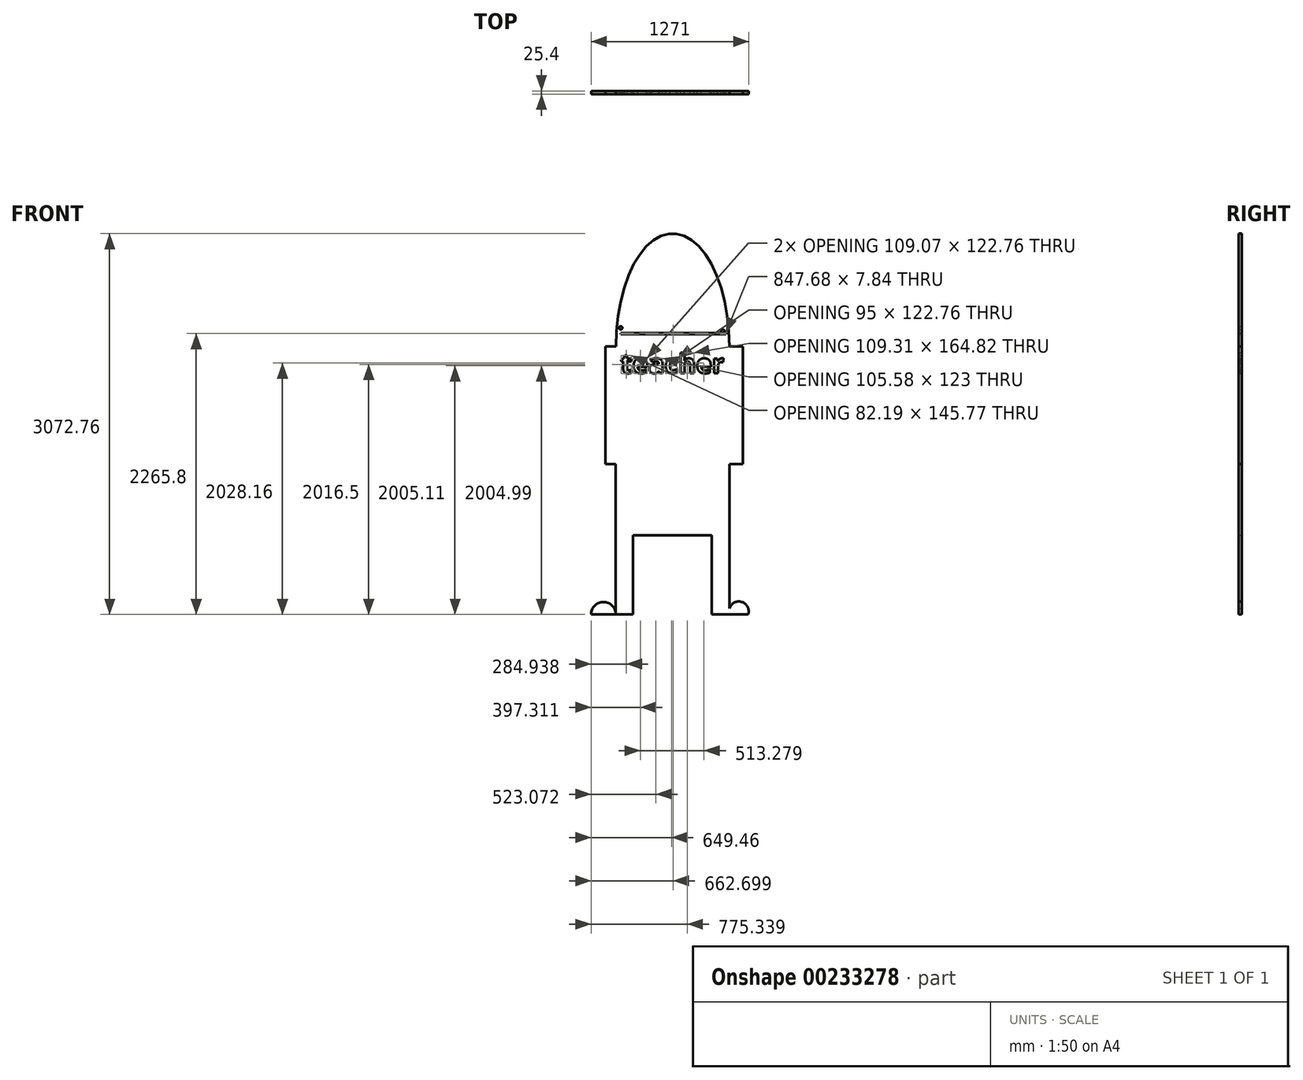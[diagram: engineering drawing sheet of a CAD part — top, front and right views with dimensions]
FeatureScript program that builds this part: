
annotation { "Feature Type Name" : "Feature", "Feature Type Description" : "" }
export const myFeature = defineFeature(function(context is Context, id is Id, definition is map)
    precondition{}
    {
        {
            var Q0;
            Q0=qCreatedBy(makeId("Front.planeOp"),FACE);
            var sketch = newSketch(context, id + "F0", { "sketchPlane" : qUnion([Q0])});
            skLineSegment(sketch, "E0.bottom", {"start": v(-39.26, 1493.2) * mm, "end": v(876.39, 1493.2) * mm});
            skLineSegment(sketch, "E0.top", {"start": v(97.58, -30.8) * mm, "end": v(733.95, -30.8) * mm});
            skLineSegment(sketch, "E0.left", {"start": v(-39.26, 1493.2) * mm, "end": v(-39.26, -30.8) * mm});
            skLineSegment(sketch, "E0.right", {"start": v(876.39, 1493.2) * mm, "end": v(876.39, -30.8) * mm});
            skEllipticalArc(sketch, "E1", {});
            skCircle(sketch, "E2", {"center": v(0, 1644.26) * mm, "radius": 13.25 * mm});
            skCircle(sketch, "E3", {"center": v(822.32, 1618.19) * mm, "radius": 13.96 * mm});
            skLineSegment(sketch, "E4.bottom", {"start": v(0, 1602.27) * mm, "end": v(847.68, 1602.27) * mm});
            skLineSegment(sketch, "E4.top", {"start": v(0, 1594.43) * mm, "end": v(847.68, 1594.43) * mm});
            skLineSegment(sketch, "E4.left", {"start": v(0, 1602.27) * mm, "end": v(0, 1594.43) * mm});
            skLineSegment(sketch, "E4.right", {"start": v(847.68, 1602.27) * mm, "end": v(847.68, 1594.43) * mm});
            skText(sketch, "E5", { "text": "teacher", "fontName": "OpenSans-Bold.ttf"});
            skLineSegment(sketch, "E6.top", {"start": v(-39.26, -667.45) * mm, "end": v(97.58, -667.45) * mm});
            skLineSegment(sketch, "E6.left", {"start": v(-39.26, -30.8) * mm, "end": v(-39.26, -667.45) * mm});
            skLineSegment(sketch, "E6.right", {"start": v(97.58, -30.8) * mm, "end": v(97.58, -667.45) * mm});
            skLineSegment(sketch, "E7.top", {"start": v(876.39, -667.45) * mm, "end": v(733.95, -667.45) * mm});
            skLineSegment(sketch, "E7.left", {"start": v(876.39, -30.8) * mm, "end": v(876.39, -619.77) * mm});
            skLineSegment(sketch, "E7.right", {"start": v(733.95, -30.8) * mm, "end": v(733.95, -667.45) * mm});
            skArc(sketch, "E8", {"start": v(-39.26, -667.45) * mm, "mid": v(-139.06, -567.64) * mm, "end": v(-238.86, -667.45) * mm});
            skArc(sketch, "E9", {"start": v(1028.49, -667.45) * mm, "mid": v(976.27, -567.56) * mm, "end": v(876.39, -619.77) * mm});
            skLineSegment(sketch, "E10", {"start": v(876.39, -667.45) * mm, "end": v(1028.49, -667.45) * mm});
            skLineSegment(sketch, "E11", {"start": v(-238.86, -667.45) * mm, "end": v(-39.26, -667.45) * mm});
            skLineSegment(sketch, "E12.bottom", {"start": v(-39.26, 545.33) * mm, "end": v(-124.85, 545.33) * mm});
            skLineSegment(sketch, "E12.top", {"start": v(-39.26, 1494.1) * mm, "end": v(-124.85, 1494.1) * mm});
            skLineSegment(sketch, "E12.left", {"start": v(-39.26, 545.33) * mm, "end": v(-39.26, 1494.1) * mm});
            skLineSegment(sketch, "E12.right", {"start": v(-124.85, 545.33) * mm, "end": v(-124.85, 1494.1) * mm});
            skLineSegment(sketch, "E13.bottom", {"start": v(876.39, 1493.2) * mm, "end": v(983.4, 1493.2) * mm});
            skLineSegment(sketch, "E13.top", {"start": v(876.39, 545.33) * mm, "end": v(983.4, 545.33) * mm});
            skLineSegment(sketch, "E13.left", {"start": v(876.39, 1493.2) * mm, "end": v(876.39, 545.33) * mm});
            skLineSegment(sketch, "E13.right", {"start": v(983.4, 1493.2) * mm, "end": v(983.4, 545.33) * mm});
            const initialGuessF0  = {"E1": [0.4185648615777492, 1.4932061264067888, 0, 1, 0.9121043746761957, 0.4569383132576944, 4.71238898038469, 1.5707963267948966], "E5": [0, 1.2783, 1, 0, 0.15618]};
            skSetInitialGuess(sketch, initialGuessF0);
            skSolve(sketch);
        }
        {
            var Q0;
            Q0 = qSketchRegion(id + "F0", true);
            extrude(context, id + "F1", {"entities" : qUnion([Q0]), "depth" : 25.4 * mm});
        }
    });
